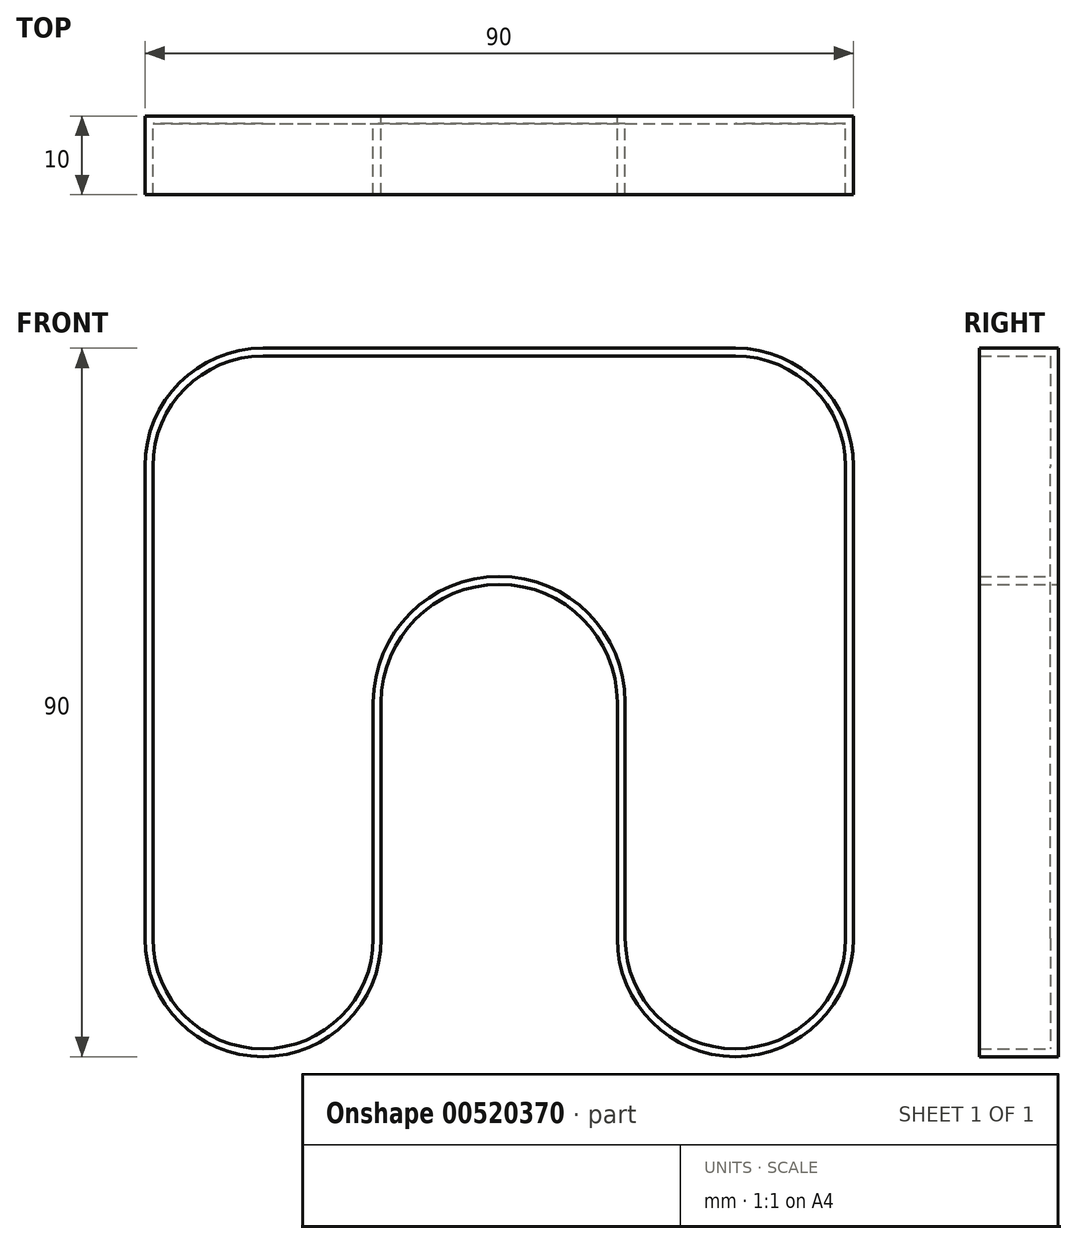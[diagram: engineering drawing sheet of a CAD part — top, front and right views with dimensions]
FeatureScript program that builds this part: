
annotation { "Feature Type Name" : "Feature", "Feature Type Description" : "" }
export const myFeature = defineFeature(function(context is Context, id is Id, definition is map)
    precondition{}
    {
        {
            var Q0;
            Q0=qCreatedBy(makeId("Front.planeOp"),FACE);
            var sketch = newSketch(context, id + "F0", { "sketchPlane" : qUnion([Q0])});
            skLineSegment(sketch, "E0", {"start": v(15, 0) * mm, "end": v(75, 0) * mm});
            skLineSegment(sketch, "E1", {"start": v(90, -15) * mm, "end": v(90, -75) * mm});
            skLineSegment(sketch, "E2", {"start": v(75, -90) * mm, "end": v(75, -90) * mm});
            skLineSegment(sketch, "E3", {"start": v(0, -75) * mm, "end": v(0, -15) * mm});
            skLineSegment(sketch, "E4", {"start": v(30, -75) * mm, "end": v(30, -45) * mm});
            skLineSegment(sketch, "E5", {"start": v(45, -30) * mm, "end": v(45, -30) * mm});
            skLineSegment(sketch, "E6", {"start": v(60, -45) * mm, "end": v(60, -75) * mm});
            skLineSegment(sketch, "E7.trimOffspring", {"start": v(15, -90) * mm, "end": v(15, -90) * mm});
            skPoint(sketch, "E8.visualSharp", {"position": v(0, 0) * mm});
            skArc(sketch, "E8.filletArc", {"start": v(15, 0) * mm, "mid": v(4.4, -4.4) * mm, "end": v(0, -15) * mm});
            skPoint(sketch, "E9.visualSharp", {"position": v(90, 0) * mm});
            skArc(sketch, "E9.filletArc", {"start": v(90, -15) * mm, "mid": v(85.6, -4.4) * mm, "end": v(75, 0) * mm});
            skPoint(sketch, "E10.visualSharp", {"position": v(90, -90) * mm});
            skArc(sketch, "E10.filletArc", {"start": v(75, -90) * mm, "mid": v(85.6, -85.6) * mm, "end": v(90, -75) * mm});
            skPoint(sketch, "E11.visualSharp", {"position": v(60, -90) * mm});
            skArc(sketch, "E11.filletArc", {"start": v(60, -75) * mm, "mid": v(64.4, -85.6) * mm, "end": v(75, -90) * mm});
            skPoint(sketch, "E12.visualSharp", {"position": v(60, -30) * mm});
            skArc(sketch, "E12.filletArc", {"start": v(60, -45) * mm, "mid": v(55.6, -34.4) * mm, "end": v(45, -30) * mm});
            skPoint(sketch, "E13.visualSharp", {"position": v(30, -30) * mm});
            skPoint(sketch, "E14.visualSharp", {"position": v(30, -90) * mm});
            skArc(sketch, "E14.filletArc", {"start": v(15, -90) * mm, "mid": v(25.6, -85.6) * mm, "end": v(30, -75) * mm});
            skPoint(sketch, "E15.visualSharp", {"position": v(0, -90) * mm});
            skArc(sketch, "E15.filletArc", {"start": v(0, -75) * mm, "mid": v(4.4, -85.6) * mm, "end": v(15, -90) * mm});
            skArc(sketch, "E16.filletArc", {"start": v(45, -30) * mm, "mid": v(34.4, -34.4) * mm, "end": v(30, -45) * mm});
            skSolve(sketch);
        }
        {
            var Q0;
            Q0=makeQuery(id+"F0.imprint","IMPRINT",FACE,{"disambiguationData":[TD([[makeQuery(id+"F0.imprint","IMPRINT",EDGE,{"derivedFrom":sQuery(id+"F0.wireOp",EDGE,"E0")}),-1.0]])]});
            extrude(context, id + "F1", {"entities" : qUnion([Q0]), "depth" : 10 * mm, "offsetDistance" : 25 * mm});
        }
        {
            var Q0;
            Q0=makeQuery(id+"F1.opExtrude","CAP_FACE",FACE,{"disambiguationData":[OSD([sQuery(id+"F0.wireOp",EDGE,"E0"),sQuery(id+"F0.wireOp",EDGE,"E1"),sQuery(id+"F0.wireOp",EDGE,"E3"),sQuery(id+"F0.wireOp",EDGE,"E4"),sQuery(id+"F0.wireOp",EDGE,"E6"),sQuery(id+"F0.wireOp",EDGE,"E8.filletArc"),sQuery(id+"F0.wireOp",EDGE,"E9.filletArc"),sQuery(id+"F0.wireOp",EDGE,"E10.filletArc"),sQuery(id+"F0.wireOp",EDGE,"E11.filletArc"),sQuery(id+"F0.wireOp",EDGE,"E12.filletArc"),sQuery(id+"F0.wireOp",EDGE,"E14.filletArc"),sQuery(id+"F0.wireOp",EDGE,"E15.filletArc"),sQuery(id+"F0.wireOp",EDGE,"E16.filletArc")])],"isStart":false});
            shell(context, id + "F2", {"entities" : qUnion([Q0]), "thickness" : 1 * mm});
        }
    });
